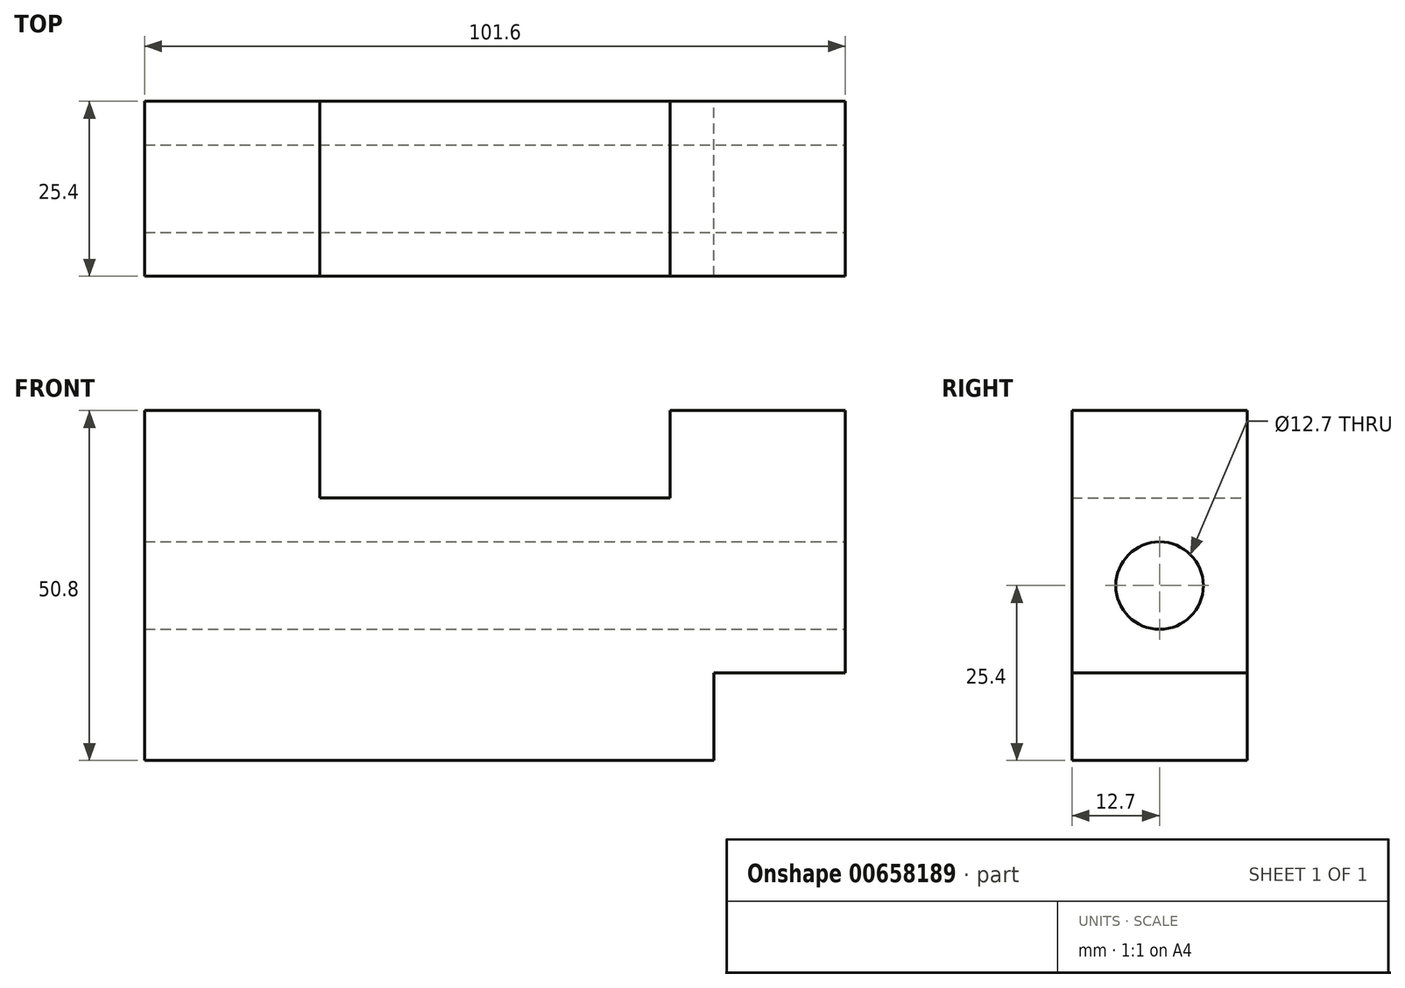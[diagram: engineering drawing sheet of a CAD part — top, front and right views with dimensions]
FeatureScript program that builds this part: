
annotation { "Feature Type Name" : "Feature", "Feature Type Description" : "" }
export const myFeature = defineFeature(function(context is Context, id is Id, definition is map)
    precondition{}
    {
        {
            var Q0;
            Q0=qCreatedBy(makeId("Front.planeOp"),FACE);
            var sketch = newSketch(context, id + "F0", { "sketchPlane" : qUnion([Q0])});
            skLineSegment(sketch, "E0.bottom", {"start": v(-68.8, 25.4) * mm, "end": v(13.75, 25.4) * mm});
            skLineSegment(sketch, "E0.top", {"start": v(-68.8, -12.7) * mm, "end": v(13.75, -12.7) * mm});
            skLineSegment(sketch, "E0.left", {"start": v(-68.8, 25.4) * mm, "end": v(-68.8, -12.7) * mm});
            skLineSegment(sketch, "E0.right", {"start": v(13.75, 25.4) * mm, "end": v(13.75, -12.7) * mm});
            skSolve(sketch);
        }
        {
            var Q0;
            Q0=qCreatedBy(makeId("Front.planeOp"),FACE);
            var sketch = newSketch(context, id + "F1", { "sketchPlane" : qUnion([Q0])});
            skLineSegment(sketch, "E1.bottom", {"start": v(-68.8, 25.4) * mm, "end": v(-43.4, 25.4) * mm});
            skLineSegment(sketch, "E1.top", {"start": v(-68.8, 38.1) * mm, "end": v(-43.4, 38.1) * mm});
            skLineSegment(sketch, "E1.left", {"start": v(-68.8, 25.4) * mm, "end": v(-68.8, 38.1) * mm});
            skLineSegment(sketch, "E1.right", {"start": v(-43.4, 25.4) * mm, "end": v(-43.4, 38.1) * mm});
            skSolve(sketch);
        }
        {
            var Q0;
            Q0=qCreatedBy(makeId("Front.planeOp"),FACE);
            var sketch = newSketch(context, id + "F2", { "sketchPlane" : qUnion([Q0])});
            skLineSegment(sketch, "E2.bottom", {"start": v(32.8, 0) * mm, "end": v(7.4, 0) * mm});
            skLineSegment(sketch, "E2.top", {"start": v(32.8, 38.1) * mm, "end": v(7.4, 38.1) * mm});
            skLineSegment(sketch, "E2.left", {"start": v(32.8, 0) * mm, "end": v(32.8, 38.1) * mm});
            skLineSegment(sketch, "E2.right", {"start": v(7.4, 0) * mm, "end": v(7.4, 38.1) * mm});
            skSolve(sketch);
        }
        {
            var Q0;
            Q0=makeQuery(id+"F1.imprint","IMPRINT",FACE,{"disambiguationData":[TD([[makeQuery(id+"F1.imprint","IMPRINT",EDGE,{"derivedFrom":sQuery(id+"F1.wireOp",EDGE,"E1.bottom")}),1.0]])]});
            extrude(context, id + "F3", {"entities" : qUnion([Q0]), "depth" : 25.4 * mm, "offsetDistance" : 25.4 * mm});
        }
        {
            var Q0;
            Q0=makeQuery(id+"F0.imprint","IMPRINT",FACE,{"disambiguationData":[TD([[makeQuery(id+"F0.imprint","IMPRINT",EDGE,{"derivedFrom":sQuery(id+"F0.wireOp",EDGE,"E0.bottom")}),-1.0]])]});
            extrude(context, id + "F4", {"entities" : qUnion([Q0]), "operationType" : NewBodyOperationType.ADD, "depth" : 25.4 * mm, "offsetDistance" : 25.4 * mm});
        }
        {
            var Q0;
            Q0=makeQuery(id+"F2.imprint","IMPRINT",FACE,{"disambiguationData":[TD([[makeQuery(id+"F2.imprint","IMPRINT",EDGE,{"derivedFrom":sQuery(id+"F2.wireOp",EDGE,"E2.bottom")}),-1.0]])]});
            extrude(context, id + "F5", {"entities" : qUnion([Q0]), "operationType" : NewBodyOperationType.ADD, "depth" : 25.4 * mm, "offsetDistance" : 25.4 * mm});
        }
        {
            var Q0;
            Q0=makeQuery(id+"F5.opExtrude","SWEPT_FACE",FACE,{"disambiguationData":[OSD([sQuery(id+"F2.wireOp",EDGE,"E2.left")])]});
            var sketch = newSketch(context, id + "F6", { "sketchPlane" : qUnion([Q0])});
            skCircle(sketch, "E3", {"center": v(-12.7, 12.7) * mm, "radius": 6.35 * mm});
            skSolve(sketch);
        }
        {
            var Q0;
            Q0=sQuery(id+"F6.wireOp",VERTEX,"E3.center");
            var Q1;
            Q1=makeQuery(id+"F3.opExtrude","SWEPT_BODY",BODY,{"disambiguationData":[OSD([sQuery(id+"F1.wireOp",EDGE,"E1.bottom"),sQuery(id+"F1.wireOp",EDGE,"E1.top"),sQuery(id+"F1.wireOp",EDGE,"E1.left"),sQuery(id+"F1.wireOp",EDGE,"E1.right")])]});
            hole(context, id + "F7", {"style" : HoleStyle.SIMPLE, "endStyle" : HoleEndStyle.THROUGH, "holeDiameter" : 12.7 * mm, "majorDiameter" : 6.35 * mm, "isTappedThrough" : true, "tappedDepth" : 12.7 * mm, "tapClearance" : 3, "locations" : qUnion([Q0]), "scope" : qUnion([Q1])});
        }
    });
